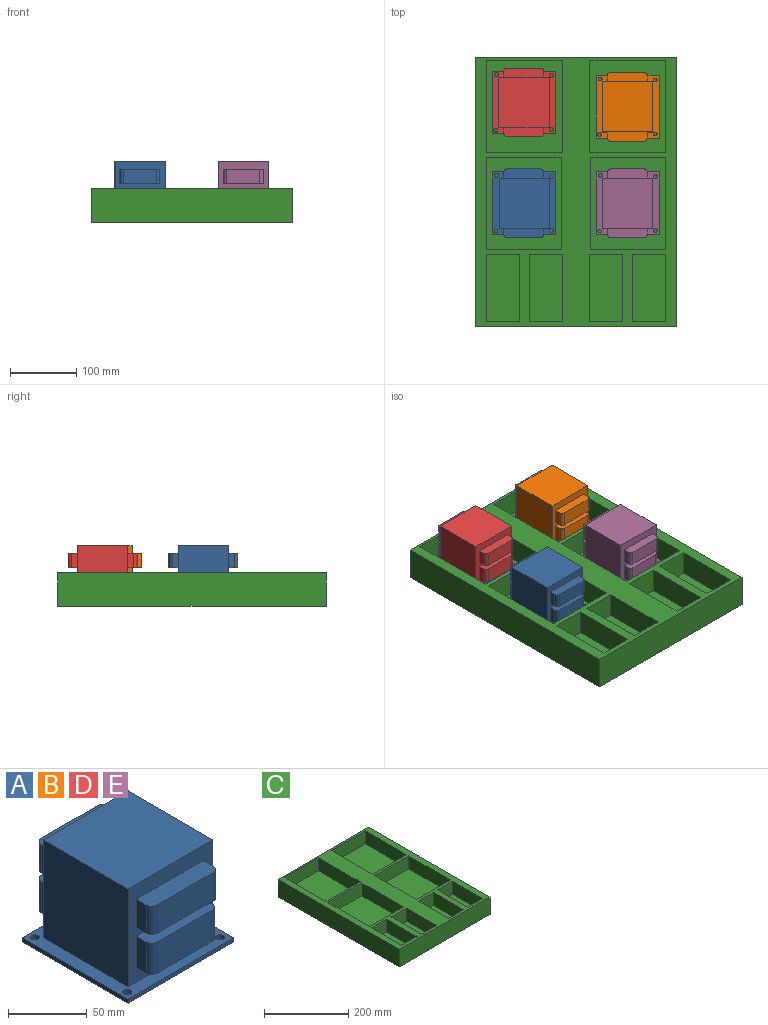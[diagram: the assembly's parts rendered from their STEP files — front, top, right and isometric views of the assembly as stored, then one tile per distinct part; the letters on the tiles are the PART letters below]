
ASSEMBLY  parts=5 mates=4
PART A: 43 faces, bbox 95.3x104.1x79.4 mm
  f0: plane 76.2x76.2mm, normal (1,0,0), area 5806.4mm2, adj f1,f3,f4,f5
  f1: plane 76.2x76.2mm, normal (0,1,0), area 3033.3mm2, adj f0,f2,f4,f5,f20,f21,f22,f23
  f2: plane 76.2x76.2mm, normal (-1,0,0), area 5806.4mm2, adj f1,f3,f4,f5
  f3: plane 76.2x76.2mm, normal (0,-1,0), area 3033.3mm2, adj f0,f2,f4,f5,f16,f17,f18,f19
  f4: plane 76.2x76.2mm, normal (0,0,1), area 5806.4mm2, adj f0,f1,f2,f3
  f5: plane 95.25x95.25mm, normal (0,0,1), area 3167.1mm2, adj f0,f1,f2,f3,f6,f7,f8,f9
  f6: plane 95.25x3.18mm, normal (1,0,0), area 302.4mm2, adj f5,f7,f9,f10
  f7: plane 95.25x3.18mm, normal (0,-1,0), area 302.4mm2, adj f5,f6,f8,f10
  f8: plane 95.25x3.18mm, normal (-1,0,0), area 302.4mm2, adj f5,f7,f9,f10
  f9: plane 95.25x3.18mm, normal (0,1,0), area 302.4mm2, adj f5,f6,f8,f10
  f10: plane 95.25x95.25mm, normal (0,0,-1), area 8973.6mm2, adj f6,f7,f8,f9,f11,f12,f13,f14
  f11: cylinder r=2.81mm len=5.61mm, axis (0,0,1), area 56mm2, adj f5,f10
  f12: cylinder r=2.81mm len=5.61mm, axis (0,0,1), area 56mm2, adj f5,f10
  f13: cylinder r=2.81mm len=5.61mm, axis (0,0,1), area 56mm2, adj f5,f10
  f14: cylinder r=2.81mm len=5.61mm, axis (0,0,1), area 56mm2, adj f5,f10
  f15: plane 50.16x22.05mm, normal (0,-1,0), area 1106.1mm2, adj f16,f18,f41,f42
  f16: plane 60.32x13.97mm, normal (0,0,-1), area 831.6mm2, adj f3,f15,f17,f19,f41,f42
  f17: plane 22.05x8.89mm, normal (-1,0,0), area 196mm2, adj f3,f16,f18,f41
  f18: plane 60.32x13.97mm, normal (0,0,1), area 831.6mm2, adj f3,f15,f17,f19,f41,f42
  f19: plane 22.05x8.89mm, normal (1,0,0), area 196mm2, adj f3,f16,f18,f42
  f20: plane 22.05x8.89mm, normal (1,0,0), area 196mm2, adj f1,f21,f23,f40
  f21: plane 60.32x13.97mm, normal (0,0,1), area 831.6mm2, adj f1,f20,f22,f24,f39,f40
  f22: plane 22.05x8.89mm, normal (-1,0,0), area 196mm2, adj f1,f21,f23,f39
  f23: plane 60.32x13.97mm, normal (0,0,-1), area 831.6mm2, adj f1,f20,f22,f24,f39,f40
  f24: plane 50.16x22.05mm, normal (0,1,0), area 1106.1mm2, adj f21,f23,f39,f40
  f25: plane 49.15x24.33mm, normal (0,-1,0), area 1195.8mm2, adj f26,f28,f37,f38
  f26: plane 59.31x13.97mm, normal (0,0,-1), area 817.5mm2, adj f3,f25,f27,f29,f37,f38
  f27: plane 24.33x8.89mm, normal (-1,0,0), area 216.3mm2, adj f3,f26,f28,f37
  f28: plane 59.31x13.97mm, normal (0,0,1), area 817.5mm2, adj f3,f25,f27,f29,f37,f38
  f29: plane 24.33x8.89mm, normal (1,0,0), area 216.3mm2, adj f3,f26,f28,f38
  f30: plane 24.33x8.89mm, normal (1,0,0), area 216.3mm2, adj f1,f31,f33,f36
  f31: plane 59.31x13.97mm, normal (0,0,1), area 817.5mm2, adj f1,f30,f32,f34,f35,f36
  f32: plane 24.33x8.89mm, normal (-1,0,0), area 216.3mm2, adj f1,f31,f33,f35
  f33: plane 59.31x13.97mm, normal (0,0,-1), area 817.5mm2, adj f1,f30,f32,f34,f35,f36
  f34: plane 49.15x24.33mm, normal (0,1,0), area 1195.8mm2, adj f31,f33,f35,f36
  f35: cylinder r=5.08mm len=24.33mm, axis (0,0,-1), area 194.2mm2, adj f31,f32,f33,f34
  f36: cylinder r=5.08mm len=24.33mm, axis (0,0,1), area 194.2mm2, adj f30,f31,f33,f34
  f37: cylinder r=5.08mm len=24.33mm, axis (0,0,1), area 194.2mm2, adj f25,f26,f27,f28
  f38: cylinder r=5.08mm len=24.33mm, axis (0,0,-1), area 194.2mm2, adj f25,f26,f28,f29
  f39: cylinder r=5.08mm len=22.05mm, axis (0,0,-1), area 176mm2, adj f21,f22,f23,f24
  f40: cylinder r=5.08mm len=22.05mm, axis (0,0,1), area 176mm2, adj f20,f21,f23,f24
  f41: cylinder r=5.08mm len=22.05mm, axis (0,0,1), area 176mm2, adj f15,f16,f17,f18
  f42: cylinder r=5.08mm len=22.05mm, axis (0,0,-1), area 176mm2, adj f15,f16,f18,f19
PART B: same geometry as A
PART C: 46 faces, bbox 304.8x406.4x50.8 mm
  f0: plane 406.4x304.8mm, normal (0,0,1), area 39354.8mm2, adj f1,f2,f3,f4,f6,f7,f8,f9
  f1: plane 304.8x50.8mm, normal (0,1,0), area 15483.8mm2, adj f0,f2,f4,f5
  f2: plane 406.4x50.8mm, normal (-1,0,0), area 20645.1mm2, adj f0,f1,f3,f5
  f3: plane 304.8x50.8mm, normal (0,-1,0), area 15483.8mm2, adj f0,f2,f4,f5
  f4: plane 406.4x50.8mm, normal (1,0,0), area 20645.1mm2, adj f0,f1,f3,f5
  f5: plane 406.4x304.8mm, normal (0,0,-1), area 123870.7mm2, adj f1,f2,f3,f4
  f6: plane 114.3x38.1mm, normal (0,-1,0), area 4354.8mm2, adj f0,f7,f9,f10
  f7: plane 139.7x38.1mm, normal (1,0,0), area 5322.6mm2, adj f0,f6,f8,f10
  f8: plane 114.3x38.1mm, normal (0,1,0), area 4354.8mm2, adj f0,f7,f9,f10
  f9: plane 139.7x38.1mm, normal (-1,0,0), area 5322.6mm2, adj f0,f6,f8,f10
  f10: plane 139.7x114.3mm, normal (0,0,1), area 15967.7mm2, adj f6,f7,f8,f9
  f11: plane 101.6x38.1mm, normal (-1,0,0), area 3871mm2, adj f0,f12,f14,f15
  f12: plane 50.8x38.1mm, normal (0,-1,0), area 1935.5mm2, adj f0,f11,f13,f15
  f13: plane 101.6x38.1mm, normal (1,0,0), area 3871mm2, adj f0,f12,f14,f15
  f14: plane 50.8x38.1mm, normal (0,1,0), area 1935.5mm2, adj f0,f11,f13,f15
  f15: plane 101.6x50.8mm, normal (0,0,1), area 5161.3mm2, adj f11,f12,f13,f14
  f16: plane 114.3x38.1mm, normal (0,1,0), area 4354.8mm2, adj f0,f17,f19,f20
  f17: plane 139.7x38.1mm, normal (-1,0,0), area 5322.6mm2, adj f0,f16,f18,f20
  f18: plane 114.3x38.1mm, normal (0,-1,0), area 4354.8mm2, adj f0,f17,f19,f20
  f19: plane 139.7x38.1mm, normal (1,0,0), area 5322.6mm2, adj f0,f16,f18,f20
  f20: plane 139.7x114.3mm, normal (0,0,1), area 15967.7mm2, adj f16,f17,f18,f19
  f21: plane 101.6x38.1mm, normal (-1,0,0), area 3871mm2, adj f0,f22,f24,f25
  f22: plane 50.8x38.1mm, normal (0,-1,0), area 1935.5mm2, adj f0,f21,f23,f25
  f23: plane 101.6x38.1mm, normal (1,0,0), area 3871mm2, adj f0,f22,f24,f25
  f24: plane 50.8x38.1mm, normal (0,1,0), area 1935.5mm2, adj f0,f21,f23,f25
  f25: plane 101.6x50.8mm, normal (0,0,1), area 5161.3mm2, adj f21,f22,f23,f24
  f26: plane 114.3x38.1mm, normal (0,-1,0), area 4354.8mm2, adj f0,f27,f29,f30
  f27: plane 139.7x38.1mm, normal (1,0,0), area 5322.6mm2, adj f0,f26,f28,f30
  f28: plane 114.3x38.1mm, normal (0,1,0), area 4354.8mm2, adj f0,f27,f29,f30
  f29: plane 139.7x38.1mm, normal (-1,0,0), area 5322.6mm2, adj f0,f26,f28,f30
  f30: plane 139.7x114.3mm, normal (0,0,1), area 15967.7mm2, adj f26,f27,f28,f29
  f31: plane 50.8x38.1mm, normal (0,-1,0), area 1935.5mm2, adj f0,f32,f34,f35
  f32: plane 101.6x38.1mm, normal (1,0,0), area 3871mm2, adj f0,f31,f33,f35
  f33: plane 50.8x38.1mm, normal (0,1,0), area 1935.5mm2, adj f0,f32,f34,f35
  f34: plane 101.6x38.1mm, normal (-1,0,0), area 3871mm2, adj f0,f31,f33,f35
  f35: plane 101.6x50.8mm, normal (0,0,1), area 5161.3mm2, adj f31,f32,f33,f34
  f36: plane 50.8x38.1mm, normal (0,-1,0), area 1935.5mm2, adj f0,f37,f39,f40
  f37: plane 101.6x38.1mm, normal (1,0,0), area 3871mm2, adj f0,f36,f38,f40
  f38: plane 50.8x38.1mm, normal (0,1,0), area 1935.5mm2, adj f0,f37,f39,f40
  f39: plane 101.6x38.1mm, normal (-1,0,0), area 3871mm2, adj f0,f36,f38,f40
  f40: plane 101.6x50.8mm, normal (0,0,1), area 5161.3mm2, adj f36,f37,f38,f39
  f41: plane 139.7x38.1mm, normal (-1,0,0), area 5322.6mm2, adj f0,f42,f44,f45
  f42: plane 114.3x38.1mm, normal (0,-1,0), area 4354.8mm2, adj f0,f41,f43,f45
  f43: plane 139.7x38.1mm, normal (1,0,0), area 5322.6mm2, adj f0,f42,f44,f45
  f44: plane 114.3x38.1mm, normal (0,1,0), area 4354.8mm2, adj f0,f41,f43,f45
  f45: plane 139.7x114.3mm, normal (0,0,1), area 15967.7mm2, adj f41,f42,f43,f44
PART D: same geometry as A
PART E: same geometry as A
PLACE A t=(-359.15,-85.62,118.19)mm
PLACE B t=(-202.33,60.54,118.19)mm
PLACE C t=(-280.64,-68.43,102.31)mm fixed
PLACE D t=(-359.43,67.23,118.19)mm
PLACE E t=(-202.12,-85.62,118.19)mm
MATE planar C.f20 <-> E.f10  axis (0,0,1) through (-202.12,-85.62,115.01)mm
MATE planar C.f10 <-> D.f10  axis (0,0,1) through (-358.95,60.54,115.01)mm
MATE planar C.f45 <-> B.f10  axis (0,0,1) through (-202.32,60.54,115.01)mm
MATE planar C.f30 <-> A.f10  axis (0,0,1) through (-359.15,-85.62,115.01)mm
